# Revit family: 0030442
name_source: partatom
category: Lighting Fixtures
revit_build: Autodesk Revit 2017 (Build: 20190507_1515(x64)
units: mm (PartAtom-declared; Revit-internal decimal feet)

## family parameters
Cut with Voids When Loaded = No
Host = Face
Light Source = Yes
OmniClass Number = 23.80.70.00
OmniClass Title = Lighting
Part Type = Normal
Room Calculation Point = No
Round Connector Dimension = Use Diameter
Shared = No

## types (2) — shared parameters
Apparent Load = 9 VA
Assembly Code = D5020200
AssetType = Fixed
ClassificationName = Uniclass2015
ClassificationValue = EF_70_80
Color Filter = 16777215
Default Elevation = 1219 mm
DiameterRecess_SYL = 140 mm  [stored 0.459318 ft]
DiameterTopBase_SYL = 140 mm  [stored 0.459318 ft]
DiameterTop_SYL = 100 mm  [stored 0.328084 ft]
Diameter_SYL = 195 mm  [stored 0.639764 ft]
Dimming Lamp Color Temperature Shift = <None>
DocumentationLiterature = http://www.sylvania-lighting.com
DurationUnit = hours
ElectricShockClassification = Class II
Emit Shape Visible in Rendering = No
Emit from Circle Diameter = 155 mm  [stored 0.50853 ft]
ExpectedLife = 50000
HeightBezel_SYL = 3 mm  [stored 0.00984252 ft]
Height_SYL = 50 mm  [stored 0.164042 ft]
IfcExportAs = IfcLightFixtureType
IfcExportType = IfcLightFixtureType
ImpactProtectionIndex = IK07
IngressProtection = IP44/20
Keynote = 16500
Lamp = LED
LampColourRenderingIndex = 80
LampMacAdamStep = 5
LampsType = LED
Manufacturer = Feilo Sylvania
ManufacturerName = Feilo Sylvania
Material = aluminium housing
Material_1_FEILO = Trim-Sylvania-STARTDownlight-White
Material_2_FEILO = Diffuser-Sylvania-STARTDownlight
Material_3_FEILO = Top-Sylvania-STARTDownlight
Material_4_FEILO = LED-Sylvania-STARTDownlight
NominalDepth = 195 mm  [stored 0.639764 ft]
NominalHeight = 50 mm  [stored 0.164042 ft]
NominalLength = 195 mm  [stored 0.639764 ft]
PowerConsumption = 9 W
PowerFactor = 0.9
RadiusReflector_SYL = 85 mm  [stored 0.278871 ft]
RadiusTop_SYL = 6 mm  [stored 0.019685 ft]
Size1_SYL = No
Size2_SYL = Yes
Size3PIR_SYL = No
Size4_SYL = No
Tilt Angle = -90.00°
Type Image = <None>
URL = http://www.sylvania-lighting.com
VisibilityPIR_SYL = No
Voltage = 0 V
Weight = 6.612 kg
WidthBezel_SYL = 30 mm  [stored 0.0984252 ft]
zero-valued in all types: Cost

## per-type parameters (varying)
| type | LampColourTemperature | LampNominalLuminous | LuminousEfficacy | Model | ModelNumber | ModelReference | Name | Photometric Web File | TypeName |
| 0030443 INSAVER SLIM UGR19 175 IP44 1075 840 WB | 4000 K | 1075 lm | 119 lm/W | Insaver Slim UGR19 175 IP44 1075lm 840 wide bezel | 0030443 | Insaver Slim UGR19 175 IP44 1075lm 840 wide bezel | Insaver Slim UGR19 175 IP44 1075lm 840 wide bezel | 0030443.ies | Insaver Slim UGR19 175 IP44 1075lm 840 wide bezel |
| 0030442 INSAVER SLIM UGR19 175 IP44 1050 830 WB | 3000 K | 1050 lm | 117 lm/W | Insaver Slim UGR19 175 IP44 1050lm 830 wide bezel | 0030442 | Insaver Slim UGR19 175 IP44 1050lm 830 wide bezel | Insaver Slim UGR19 175 IP44 1050lm 830 wide bezel | 0030442.ies | Insaver Slim UGR19 175 IP44 1050lm 830 wide bezel |

note: [stored X ft] marks values corroborated as IEEE doubles in the binary element streams (Revit-internal decimal feet)

## geometry (parser evidence)
native form markers: Sweep x2
no freeform markers — native parametric forms only
